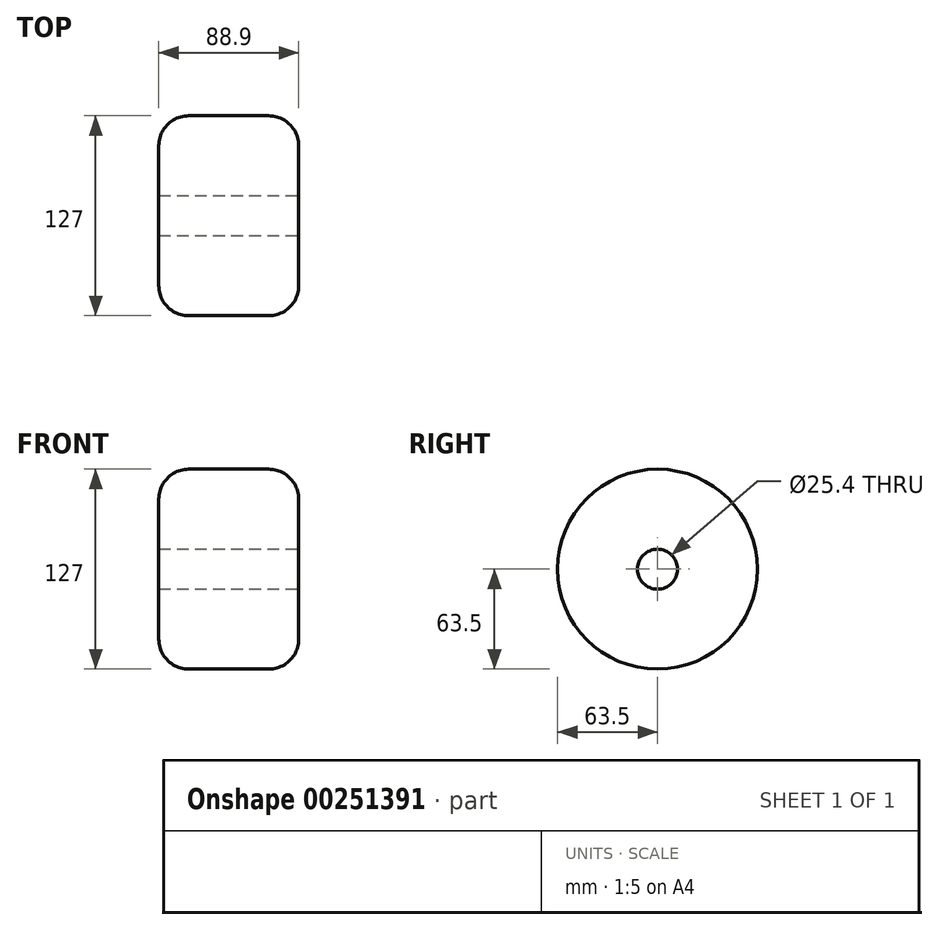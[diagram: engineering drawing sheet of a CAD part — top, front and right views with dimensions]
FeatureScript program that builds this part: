
annotation { "Feature Type Name" : "Feature", "Feature Type Description" : "" }
export const myFeature = defineFeature(function(context is Context, id is Id, definition is map)
    precondition{}
    {
        {
            var Q0;
            Q0=qCreatedBy(makeId("Right.planeOp"),FACE);
            var sketch = newSketch(context, id + "F0", { "sketchPlane" : qUnion([Q0])});
            skCircle(sketch, "E0", {"center": v(0, 0) * mm, "radius": 63.5 * mm});
            skSolve(sketch);
        }
        {
            var Q0;
            Q0=makeQuery(id+"F0.imprint","IMPRINT",FACE,{"disambiguationData":[TD([[makeQuery(id+"F0.imprint","IMPRINT",EDGE,{"derivedFrom":sQuery(id+"F0.wireOp",EDGE,"E0")}),1.0]])]});
            extrude(context, id + "F1", {"entities" : qUnion([Q0]), "depth" : 88.9 * mm});
        }
        {
            var Q0;
            Q0=makeQuery(id+"F1.opExtrude","CAP_EDGE",EDGE,{"disambiguationData":[OSD([sQuery(id+"F0.wireOp",EDGE,"E0")])],"isStart":true});
            var Q1;
            Q1=makeQuery(id+"F1.opExtrude","SWEPT_FACE",FACE,{"disambiguationData":[OSD([sQuery(id+"F0.wireOp",EDGE,"E0")])]});
            fillet(context, id + "F2", {"entities" : qUnion([Q0, Q1]), "radius" : 19.05 * mm, "tangentPropagation" : true, "allowEdgeOverflow" : false});
        }
        {
            var Q0;
            Q0=makeQuery(id+"F1.opExtrude","CAP_FACE",FACE,{"disambiguationData":[OSD([sQuery(id+"F0.wireOp",EDGE,"E0")])],"isStart":false});
            var sketch = newSketch(context, id + "F3", { "sketchPlane" : qUnion([Q0])});
            skCircle(sketch, "E1", {"center": v(0, 0) * mm, "radius": 12.7 * mm});
            skSolve(sketch);
        }
        {
            var Q0;
            Q0=makeQuery(id+"F3.imprint","IMPRINT",FACE,{"disambiguationData":[TD([[makeQuery(id+"F3.imprint","IMPRINT",EDGE,{"derivedFrom":sQuery(id+"F3.wireOp",EDGE,"E1")}),1.0]])]});
            extrude(context, id + "F4", {"entities" : qUnion([Q0]), "operationType" : NewBodyOperationType.REMOVE, "endBound" : BoundingType.THROUGH_ALL, "oppositeDirection" : true, "depth" : 25.4 * mm});
        }
    });
